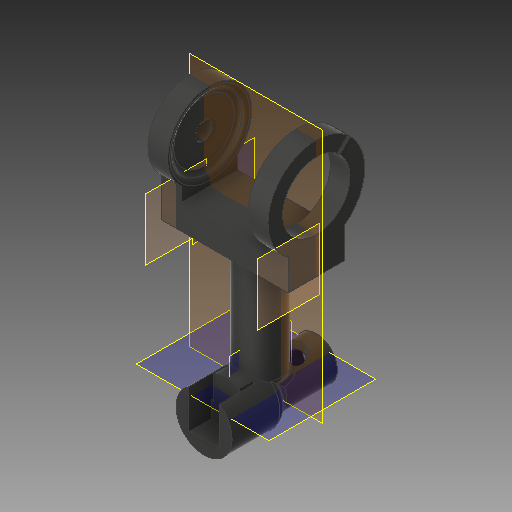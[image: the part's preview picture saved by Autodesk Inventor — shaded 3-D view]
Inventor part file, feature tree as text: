
AUTODESK INVENTOR PART (.ipt)
format: ipt  version: 2018 (Build 220112000, 112)  size: 543,744 bytes
history: native  units: mm
features: extrude x23, sketch x21, plane x6, fillet x5, move_body x3, direct_edit x2, other x1
ambient origin geometry x8: Origin, YZ Plane, XZ Plane, XY Plane, X Axis, Y Axis, Z Axis, Center Point
bodies: Body1 (feature_tree)
feature tree (61):
  other  "Sólido1"
  extrude  "Extrusión1"  Depth=20.0mm
  plane  "Plano de trabajo1"
  plane  "Plano de trabajo2"
  extrude  "Extrusión8"  Depth=24.5mm
  plane  "Plano de trabajo3"
  plane  "Plano de trabajo4"
  plane  "Plano de trabajo5"
  extrude  "Extrusión10"  Depth=10.0mm
  plane  "Plano de trabajo6"
  extrude  "Extrusión12"  Depth=5.0mm TaperAngle=0.0deg
  extrude  "Extrusión13"  Depth=6.3mm
  extrude  "Extrusión14"  Depth=24.5mm
  extrude  "Extrusión15"  Depth=1.6mm
  extrude  "Extrusión16"  Depth=20.0mm
  extrude  "Extrusión17"  Depth=15.0mm
  extrude  "Extrusión18"  Depth=3.0mm
  fillet  "Empalme4"  Radius=2.0mm
  extrude  "Extrusión19"  Depth=2.0mm
  fillet  "Empalme5"  Radius=2.0mm
  sketch  "Boceto26"  dims[d82=2.9mm d83=7.9mm d84=0.0mm]
  sketch  "Boceto27"  dims[d90=3.0mm d99=4.0mm]
  extrude  "Extrusión23"  Depth=7.9mm TaperAngle=0.0deg
  extrude  "Extrusión26"  Depth=4.0mm
  extrude  "Extrusion27"  Depth=14.8mm
  extrude  "Extrusion29"  Depth=10.0mm TaperAngle=0.0deg
  sketch  "Sketch32"  dims[d114=15.0mm d115=20.0mm d116=0.0mm d117=10.0mm]
  fillet  "Fillet8"  Radius=10.0mm
  extrude  "Extrusion31"  Depth=10.0mm
  extrude  "Extrusion32"  Depth=5.0mm
  extrude  "Extrusion33"  Depth=0.5mm
  extrude  "Extrusion34"  Depth=0.8mm
  direct_edit  "Direct Edit1"
  direct_edit  "Direct Edit2"
  fillet  "Fillet9"  Radius=0.8mm
  extrude  "Extrusion35"  Depth=3.0mm TaperAngle=0.0deg
  extrude  "Extrusion36"  TaperAngle=0.0deg  [1 undecoded]
  extrude  "Extrusion37"  TaperAngle=0.0deg  [1 undecoded]
  fillet  "Fillet10"  Radius=2.0mm
  extrude  "Extrusión38"  Depth=24.0mm
  sketch  "Boceto1"  dims[d0=40.0mm d1=20.0mm]
  sketch  "Boceto8"  dims[d2=5.0mm d3=0.0mm d28=24.5mm]
  sketch  "Boceto14"  dims[d30=10.0mm d31=0.0mm d40=15.0mm]
  sketch  "Boceto17"  dims[d41=40.0mm d42=0.0mm d53=5.0mm d54=0.0mm]
  sketch  "Boceto18"  dims[d55=3.0mm d56=0.0mm d58=6.3mm]
  sketch  "Boceto19"  dims[d59=8.0mm d60=0.0mm d61=24.5mm]
  sketch  "Boceto20"  dims[d62=5.0mm d63=0.0mm d64=1.6mm]
  sketch  "Boceto21"  dims[d65=2.0mm d66=0.0mm d69=20.0mm]
  sketch  "Boceto22"  dims[d70=20.0mm d71=0.0mm d72=15.0mm]
  sketch  "Boceto23"  dims[d73=20.0mm d74=0.0mm d75=3.0mm d78=2.0mm]
  sketch  "Boceto24"  dims[d79=2.9mm d80=2.0mm d81=2.0mm]
  sketch  "Boceto28"  dims[d100=25.0mm d101=0.0mm d113=14.8mm]
  sketch  "Sketch33"  dims[d118=10.0mm d119=0.0mm d122=10.0mm]
  sketch  "Sketch34"  dims[d126=8.0mm d127=0.0mm d131=5.0mm]
  sketch  "Sketch35"  dims[d132=7.9mm d133=0.0mm d138=0.5mm]
  sketch  "Sketch36"  dims[d139=7.9mm d140=0.0mm d142=0.8mm d143=0.8mm]
  sketch  "Sketch37"  dims[d144=5.0mm d145=0.0mm d146=3.0mm d147=0.0mm]
  sketch  "Boceto38"  dims[d148=0.0mm d149=0.0mm d150=2.0mm d151=0.0mm d152=0.0mm d153=-3.0mm d154=0.0mm d155=0.0mm d156=-3.0mm d157=2.0mm d158=24.0mm d159=7.0mm d160=0.0mm d161=15.0mm d162=20.0mm d163=0.0mm d164=3.0mm d165=0.0mm d166=3.0mm d170=7.0mm d171=0.0mm]
  move_body  "Move1"
  move_body  "Move2"
  move_body  "Move3"
note: 2 required parameter values undecoded (feature->parameter linkage not recoverable at this tier; creation-order binding heuristic only, values carry confidence <= 0.55)
